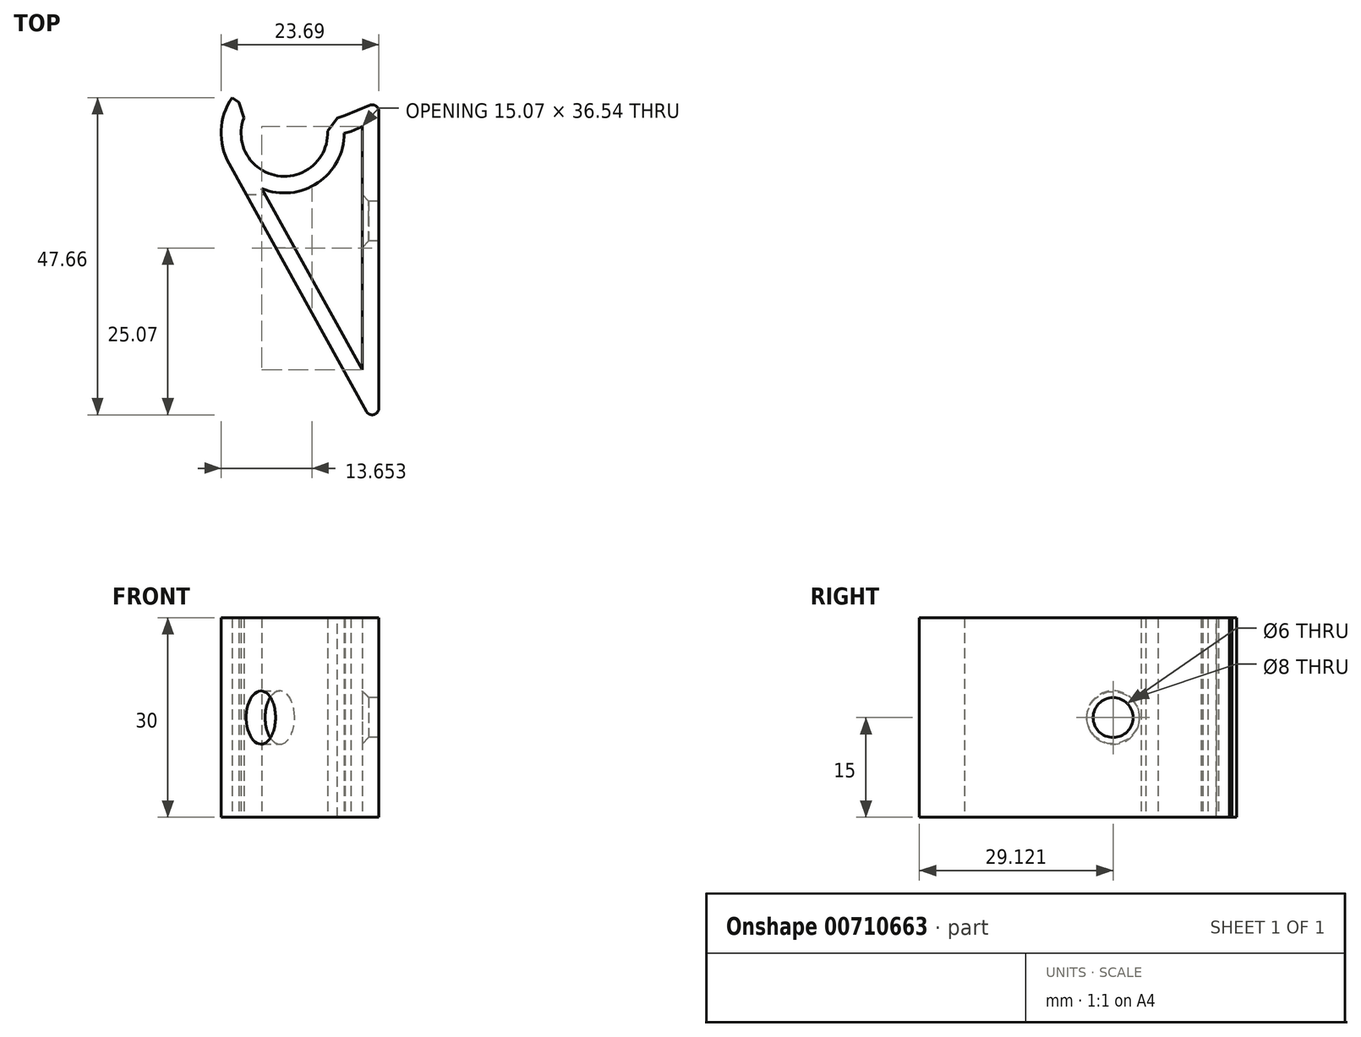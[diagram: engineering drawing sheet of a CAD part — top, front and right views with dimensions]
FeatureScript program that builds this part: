
annotation { "Feature Type Name" : "Feature", "Feature Type Description" : "" }
export const myFeature = defineFeature(function(context is Context, id is Id, definition is map)
    precondition{}
    {
        {
            var Q0;
            Q0=qCreatedBy(makeId("Top.planeOp"),FACE);
            var sketch = newSketch(context, id + "F0", { "sketchPlane" : qUnion([Q0])});
            skLineSegment(sketch, "E0", {"start": v(0, 22.27) * mm, "end": v(0, -27.73) * mm});
            skArc(sketch, "E1", {"start": v(-19.58, 21.13) * mm, "mid": v(-15.21, 11.07) * mm, "end": v(-7.94, 19.28) * mm});
            skArc(sketch, "E2", {"start": v(-22.07, 22.8) * mm, "mid": v(-15.68, 8.1) * mm, "end": v(-5.06, 20.1) * mm});
            skLineSegment(sketch, "E3", {"start": v(-14.2, 17.5) * mm, "end": v(-22.07, 22.8) * mm});
            skLineSegment(sketch, "E4", {"start": v(-14.2, 17.5) * mm, "end": v(-5.06, 20.1) * mm});
            skLineSegment(sketch, "E5", {"start": v(-5.06, 20.1) * mm, "end": v(0, 22.27) * mm});
            skLineSegment(sketch, "E6", {"start": v(0, -27.73) * mm, "end": v(-22.5, 12.89) * mm});
            skPoint(sketch, "E7", {"position": v(-19.58, 21.13) * mm});
            skPoint(sketch, "E8", {"position": v(-7.94, 19.28) * mm});
            skPoint(sketch, "E9", {"position": v(-22.07, 22.8) * mm});
            skPoint(sketch, "E10", {"position": v(-5.06, 20.1) * mm});
            skSolve(sketch);
        }
        {
            var Q0;
            Q0=makeQuery(id+"F0.imprint","IMPRINT",FACE,{"disambiguationData":[TD([[makeQuery(id+"F0.imprint","IMPRINT",EDGE,{"derivedFrom":sQuery(id+"F0.wireOp",EDGE,"E0")}),-1.0]])]});
            var Q1;
            {var subQ1=sQuery(id+"F0.wireOp",EDGE,"E1");Q1=makeQuery(id+"F0.imprint","IMPRINT",FACE,{"disambiguationData":[TD([[makeQuery(id+"F0.imprint","IMPRINT",EDGE,{"derivedFrom":subQ1}),-1.0]])]});}
            extrude(context, id + "F1", {"entities" : qUnion([Q0, Q1]), "depth" : 30 * mm, "offsetDistance" : 25 * mm});
        }
        {
            var Q0;
            Q0=makeQuery(id+"F1.opExtrude","CAP_FACE",FACE,{"disambiguationData":[OSD([sQuery(id+"F0.wireOp",EDGE,"E0"),sQuery(id+"F0.wireOp",EDGE,"E1"),sQuery(id+"F0.wireOp",EDGE,"E2"),sQuery(id+"F0.wireOp",EDGE,"E3"),sQuery(id+"F0.wireOp",EDGE,"E4"),sQuery(id+"F0.wireOp",EDGE,"E5"),sQuery(id+"F0.wireOp",EDGE,"E6")])],"isStart":false});
            shell(context, id + "F2", {"entities" : qUnion([Q0]), "thickness" : 2.5 * mm});
        }
        {
            var Q0;
            Q0=makeQuery(id+"F2.opShell","OFFSET_FACE",FACE,{"disambiguationData":[OSD([sQuery(id+"F0.wireOp",EDGE,"E0"),sQuery(id+"F0.wireOp",EDGE,"E1"),sQuery(id+"F0.wireOp",EDGE,"E2"),sQuery(id+"F0.wireOp",EDGE,"E3"),sQuery(id+"F0.wireOp",EDGE,"E4"),sQuery(id+"F0.wireOp",EDGE,"E5"),sQuery(id+"F0.wireOp",EDGE,"E6")])]});
            extrude(context, id + "F3", {"entities" : qUnion([Q0]), "operationType" : NewBodyOperationType.REMOVE, "oppositeDirection" : true, "depth" : 25 * mm, "offsetDistance" : 25 * mm});
        }
        {
            var Q0;
            Q0=makeQuery(id+"F1.opExtrude","SWEPT_EDGE",EDGE,{"disambiguationData":[OSD([sQuery(id+"F0.wireOp",EDGE,"E1"),sQuery(id+"F0.wireOp",EDGE,"E3")])]});
            var Q1;
            Q1=makeQuery(id+"F1.opExtrude","SWEPT_EDGE",EDGE,{"disambiguationData":[OSD([sQuery(id+"F0.wireOp",EDGE,"E1"),sQuery(id+"F0.wireOp",EDGE,"E4")])]});
            chamfer(context, id + "F4", {"entities" : qUnion([Q0, Q1]), "width" : 2 * mm, "tangentPropagation" : true});
        }
        {
            var Q0;
            Q0=makeQuery(id+"F1.opExtrude","SWEPT_EDGE",EDGE,{"disambiguationData":[OSD([sQuery(id+"F0.wireOp",EDGE,"E0"),sQuery(id+"F0.wireOp",EDGE,"E6")])]});
            var Q1;
            Q1=makeQuery(id+"F1.opExtrude","SWEPT_EDGE",EDGE,{"disambiguationData":[OSD([sQuery(id+"F0.wireOp",EDGE,"E0"),sQuery(id+"F0.wireOp",EDGE,"E5")])]});
            fillet(context, id + "F5", {"entities" : qUnion([Q0, Q1]), "radius" : 1 * mm, "tangentPropagation" : true, "allowEdgeOverflow" : false});
        }
        {
            var Q0;
            {var subQ0=sQuery(id+"F0.wireOp",EDGE,"E0");Q0=makeQuery(id+"F3.boolean.opBoolean","MERGE",FACE,{"derivedFrom":[makeQuery(id+"F2.opShell","OFFSET_FACE",FACE,{"disambiguationData":[OSD([subQ0])]})],"fromTools":[makeQuery(id+"F3.opExtrude","SWEPT_FACE",FACE,{"disambiguationData":[OSD([subQ0])]})]});}
            var sketch = newSketch(context, id + "F6", { "sketchPlane" : qUnion([Q0])});
            skPoint(sketch, "E11", {"position": v(-4.26, 15) * mm});
            skPoint(sketch, "E11.positionSnap0", {"position": v(-18.48, 15) * mm});
            skSolve(sketch);
        }
        {
            var Q0;
            Q0=sQuery(id+"F6.wireOp",VERTEX,"E11");
            var Q1;
            Q1=makeQuery(id+"F1.opExtrude","SWEPT_BODY",BODY,{"disambiguationData":[OSD([sQuery(id+"F0.wireOp",EDGE,"E0"),sQuery(id+"F0.wireOp",EDGE,"E1"),sQuery(id+"F0.wireOp",EDGE,"E2"),sQuery(id+"F0.wireOp",EDGE,"E3"),sQuery(id+"F0.wireOp",EDGE,"E4"),sQuery(id+"F0.wireOp",EDGE,"E5"),sQuery(id+"F0.wireOp",EDGE,"E6")])]});
            hole(context, id + "F7", {"style" : HoleStyle.C_SINK, "endStyle" : HoleEndStyle.BLIND, "holeDiameter" : 6 * mm, "cSinkDiameter" : 8 * mm, "cSinkAngle" : 90 * degree, "majorDiameter" : 5 * mm, "holeDepth" : 4 * mm, "isTappedThrough" : true, "tappedDepth" : 12 * mm, "tapClearance" : 3, "startFromSketch" : true, "locations" : qUnion([Q0]), "scope" : qUnion([Q1])});
        }
        {
            var Q0;
            Q0=sQuery(id+"F6.wireOp",VERTEX,"E11");
            var Q1;
            Q1=makeQuery(id+"F1.opExtrude","SWEPT_BODY",BODY,{"disambiguationData":[OSD([sQuery(id+"F0.wireOp",EDGE,"E0"),sQuery(id+"F0.wireOp",EDGE,"E1"),sQuery(id+"F0.wireOp",EDGE,"E2"),sQuery(id+"F0.wireOp",EDGE,"E3"),sQuery(id+"F0.wireOp",EDGE,"E4"),sQuery(id+"F0.wireOp",EDGE,"E5"),sQuery(id+"F0.wireOp",EDGE,"E6")])]});
            hole(context, id + "F8", {"style" : HoleStyle.SIMPLE, "endStyle" : HoleEndStyle.THROUGH, "oppositeDirection" : true, "holeDiameter" : 8 * mm, "majorDiameter" : 5 * mm, "isTappedThrough" : true, "tappedDepth" : 12 * mm, "tapClearance" : 3, "startFromSketch" : true, "locations" : qUnion([Q0]), "scope" : qUnion([Q1])});
        }
    });
